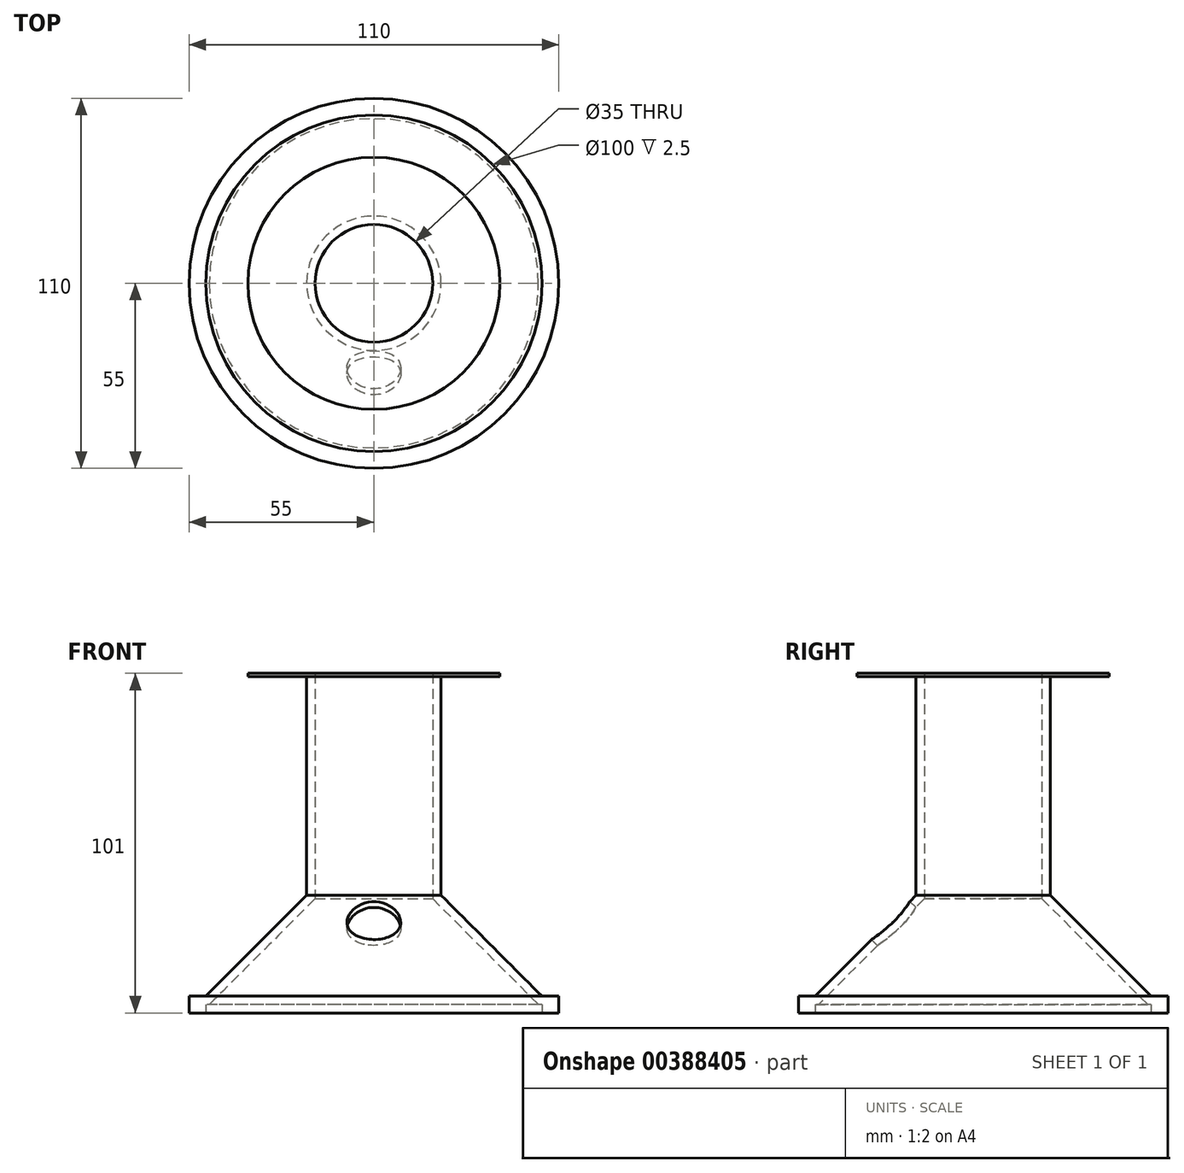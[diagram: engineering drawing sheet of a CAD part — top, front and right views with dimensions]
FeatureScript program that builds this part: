
annotation { "Feature Type Name" : "Feature", "Feature Type Description" : "" }
export const myFeature = defineFeature(function(context is Context, id is Id, definition is map)
    precondition{}
    {
        {
            var Q0;
            Q0=qCreatedBy(makeId("Top.planeOp"),FACE);
            var sketch = newSketch(context, id + "F0", { "sketchPlane" : qUnion([Q0])});
            skCircle(sketch, "E0", {"center": v(0, 0) * mm, "radius": 20 * mm});
            skCircle(sketch, "E1", {"center": v(0, 0) * mm, "radius": 50 * mm});
            skCircle(sketch, "E2", {"center": v(0, 0) * mm, "radius": 55 * mm});
            skSolve(sketch);
        }
        {
            var Q0;
            Q0=makeQuery(id+"F0.imprint","IMPRINT",FACE,{"disambiguationData":[TD([[makeQuery(id+"F0.imprint","IMPRINT",EDGE,{"derivedFrom":sQuery(id+"F0.wireOp",EDGE,"E0")}),1.0]])]});
            extrude(context, id + "F1", {"entities" : qUnion([Q0]), "depth" : 100 * mm, "offsetDistance" : 25 * mm});
        }
        {
            var Q0;
            Q0=makeQuery(id+"F0.imprint","IMPRINT",FACE,{"disambiguationData":[TD([[makeQuery(id+"F0.imprint","IMPRINT",EDGE,{"derivedFrom":sQuery(id+"F0.wireOp",EDGE,"E0")}),-1.0]])]});
            extrude(context, id + "F2", {"entities" : qUnion([Q0]), "operationType" : NewBodyOperationType.ADD, "depth" : 35 * mm, "offsetDistance" : 25 * mm});
        }
        {
            var Q0;
            Q0=makeQuery(id+"F2.opExtrude","CAP_EDGE",EDGE,{"disambiguationData":[OSD([sQuery(id+"F0.wireOp",EDGE,"E1")])],"isStart":false});
            chamfer(context, id + "F3", {"entities" : qUnion([Q0]), "width" : 30 * mm, "tangentPropagation" : true});
        }
        {
            var Q0;
            Q0=makeQuery(id+"F0.imprint","IMPRINT",FACE,{"disambiguationData":[TD([[makeQuery(id+"F0.imprint","IMPRINT",EDGE,{"derivedFrom":sQuery(id+"F0.wireOp",EDGE,"E1")}),-1.0]])]});
            extrude(context, id + "F4", {"entities" : qUnion([Q0]), "operationType" : NewBodyOperationType.ADD, "depth" : 5 * mm, "offsetDistance" : 25 * mm});
        }
        {
            var Q0;
            Q0=makeQuery(id+"F1.opExtrude","CAP_FACE",FACE,{"disambiguationData":[OSD([sQuery(id+"F0.wireOp",EDGE,"E0")])],"isStart":false});
            cPlane(context, id + "F5", {"entities" : qUnion([Q0]), "cplaneType" : CPlaneType.OFFSET, "offset" : 0 * mm, "width" : 150 * mm, "height" : 150 * mm});
        }
        {
            var Q0;
            Q0=qCreatedBy(id+"F5.planeOp",FACE);
            var sketch = newSketch(context, id + "F6", { "sketchPlane" : qUnion([Q0])});
            skCircle(sketch, "E3", {"center": v(0, 0) * mm, "radius": 37.5 * mm});
            skSolve(sketch);
        }
        {
            var Q0;
            Q0=makeQuery(id+"F6.imprint","IMPRINT",FACE,{"disambiguationData":[TD([[makeQuery(id+"F6.imprint","IMPRINT",EDGE,{"derivedFrom":sQuery(id+"F6.wireOp",EDGE,"E3")}),1.0]])]});
            extrude(context, id + "F7", {"entities" : qUnion([Q0]), "operationType" : NewBodyOperationType.ADD, "depth" : 1 * mm, "offsetDistance" : 25 * mm});
        }
        {
            var Q0;
            Q0=makeQuery(id+"F7.opExtrude","CAP_FACE",FACE,{"disambiguationData":[OSD([sQuery(id+"F6.wireOp",EDGE,"E3")])],"isStart":false});
            var Q1;
            {var subQ0=sQuery(id+"F0.wireOp",EDGE,"E1");var subQ1=sQuery(id+"F0.wireOp",EDGE,"E0");Q1=makeQuery(id+"F4.boolean.opBoolean","MERGE",FACE,{"derivedFrom":[makeQuery(id+"F2.boolean.opBoolean","MERGE",FACE,{"derivedFrom":[makeQuery(id+"F1.opExtrude","CAP_FACE",FACE,{"disambiguationData":[OSD([subQ1])],"isStart":true}),makeQuery(id+"F2.opExtrude","CAP_FACE",FACE,{"disambiguationData":[OSD([subQ1,subQ0])],"isStart":true})]}),makeQuery(id+"F4.opExtrude","CAP_FACE",FACE,{"disambiguationData":[OSD([subQ0,sQuery(id+"F0.wireOp",EDGE,"E2")])],"isStart":true})]});}
            shell(context, id + "F8", {"entities" : qUnion([Q0, Q1]), "thickness" : 2.5 * mm});
        }
        {
            var Q0;
            Q0=qCreatedBy(makeId("Top.planeOp"),FACE);
            var sketch = newSketch(context, id + "F9", { "sketchPlane" : qUnion([Q0])});
            skLineSegment(sketch, "E4", {"start": v(0, 0) * mm, "end": v(0, -55) * mm});
            skLineSegment(sketch, "E5.bottom", {"start": v(-11.29, -55) * mm, "end": v(13.8, -55) * mm});
            skLineSegment(sketch, "E5.top", {"start": v(-11.29, -51.78) * mm, "end": v(13.8, -51.78) * mm});
            skLineSegment(sketch, "E5.left", {"start": v(-11.29, -55) * mm, "end": v(-11.29, -51.78) * mm});
            skLineSegment(sketch, "E5.right", {"start": v(13.8, -55) * mm, "end": v(13.8, -51.78) * mm});
            skSolve(sketch);
        }
        {
            var Q0;
            {var subQ5=sQuery(id+"F9.wireOp",EDGE,"E5.right");Q0=makeQuery(id+"F9.imprint","IMPRINT",FACE,{"disambiguationData":[TD([[makeQuery(id+"F9.imprint","IMPRINT",EDGE,{"derivedFrom":subQ5}),1.0]])]});}
            var Q1;
            {var subQ5=sQuery(id+"F9.wireOp",EDGE,"E5.left");Q1=makeQuery(id+"F9.imprint","IMPRINT",FACE,{"disambiguationData":[TD([[makeQuery(id+"F9.imprint","IMPRINT",EDGE,{"derivedFrom":subQ5}),-1.0]])]});}
            extrude(context, id + "F10", {"entities" : qUnion([Q0, Q1]), "operationType" : NewBodyOperationType.ADD, "depth" : 22 * mm, "offsetDistance" : 25 * mm});
        }
        {
            var Q0;
            Q0=makeQuery(id+"F10.opExtrude","CAP_EDGE",EDGE,{"disambiguationData":[OSD([sQuery(id+"F9.wireOp",EDGE,"E5.bottom")])],"isStart":false});
            cPlane(context, id + "F11", {"entities" : qUnion([Q0]), "cplaneType" : CPlaneType.LINE_ANGLE, "offset" : 25 * mm, "angle" : 45 * degree, "oppositeDirection" : true, "width" : 150 * mm, "height" : 150 * mm});
        }
        {
            var Q0;
            Q0=qCreatedBy(id+"F11.planeOp",FACE);
            var sketch = newSketch(context, id + "F12", { "sketchPlane" : qUnion([Q0])});
            skCircle(sketch, "E6", {"center": v(0, 0) * mm, "radius": 8 * mm});
            skSolve(sketch);
        }
        {
            var Q0;
            Q0=makeQuery(id+"F12.imprint","IMPRINT",FACE,{"disambiguationData":[TD([[makeQuery(id+"F12.imprint","IMPRINT",EDGE,{"derivedFrom":sQuery(id+"F12.wireOp",EDGE,"E6")}),1.0]])]});
            extrude(context, id + "F13", {"entities" : qUnion([Q0]), "operationType" : NewBodyOperationType.REMOVE, "depth" : 25 * mm, "offsetDistance" : 25 * mm});
        }
        {
            var Q0;
            Q0=makeQuery(id+"F10.opExtrude","CAP_FACE",FACE,{"disambiguationData":[OSD([sQuery(id+"F9.wireOp",EDGE,"E5.bottom"),sQuery(id+"F9.wireOp",EDGE,"E5.top"),sQuery(id+"F9.wireOp",EDGE,"E5.left"),sQuery(id+"F9.wireOp",EDGE,"E5.right")])],"isStart":false});
            extrude(context, id + "F14", {"entities" : qUnion([Q0]), "operationType" : NewBodyOperationType.REMOVE, "oppositeDirection" : true, "depth" : 48.8 * mm, "offsetDistance" : 25 * mm});
        }
        {
            var Q0;
            Q0=makeQuery(id+"F0.imprint","IMPRINT",FACE,{"disambiguationData":[TD([[makeQuery(id+"F0.imprint","IMPRINT",EDGE,{"derivedFrom":sQuery(id+"F0.wireOp",EDGE,"E1")}),-1.0]])]});
            extrude(context, id + "F15", {"entities" : qUnion([Q0]), "operationType" : NewBodyOperationType.ADD, "depth" : 5 * mm, "offsetDistance" : 25 * mm});
        }
    });
